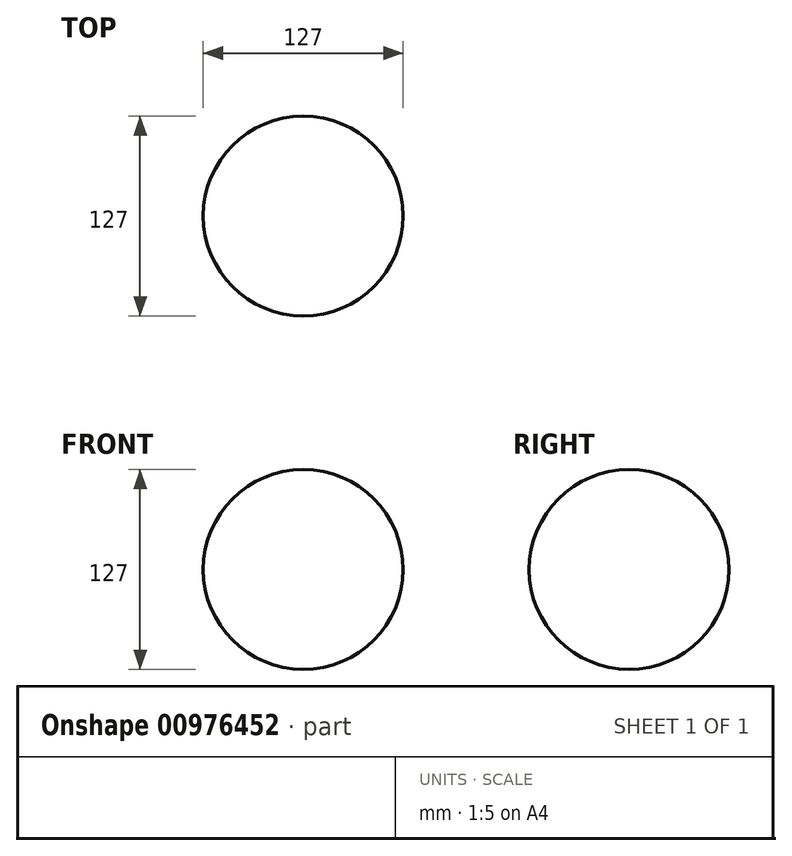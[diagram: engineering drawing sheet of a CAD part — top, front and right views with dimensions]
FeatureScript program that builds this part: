
annotation { "Feature Type Name" : "Feature", "Feature Type Description" : "" }
export const myFeature = defineFeature(function(context is Context, id is Id, definition is map)
    precondition{}
    {
        {
            var Q0;
            Q0=qCreatedBy(makeId("Front.planeOp"),FACE);
            var sketch = newSketch(context, id + "F0", { "sketchPlane" : qUnion([Q0])});
            skCircle(sketch, "E0", {"center": v(0, 0) * mm, "radius": 63.5 * mm});
            skLineSegment(sketch, "E1", {"start": v(0, 63.5) * mm, "end": v(0, -63.5) * mm});
            skSolve(sketch);
        }
        {
            var Q0;
            {var subQ0=sQuery(id+"F0.wireOp",EDGE,"E1");Q0=makeQuery(id+"F0.imprint","IMPRINT",FACE,{"disambiguationData":[TD([[makeQuery(id+"F0.imprint","IMPRINT",EDGE,{"derivedFrom":subQ0}),1.0]])]});}
            var Q1;
            Q1=sQuery(id+"F0.wireOp",EDGE,"E1");
            revolve(context, id + "F1", {"surfaceOperationType" : NewSurfaceOperationType.NEW, "entities" : qUnion([Q0]), "axis" : qUnion([Q1]), "revolveType" : RevolveType.FULL});
        }
    });
